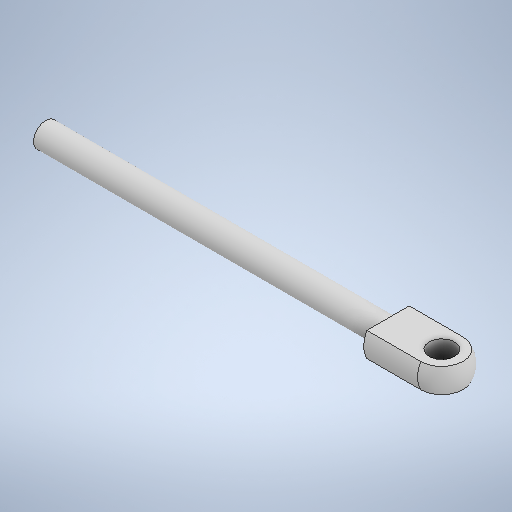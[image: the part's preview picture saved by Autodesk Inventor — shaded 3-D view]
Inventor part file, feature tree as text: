
AUTODESK INVENTOR PART (.ipt)
format: ipt  version: 2025.1 (Build 291241000, 241)  size: 287,744 bytes
history: native  units: mm
features: sketch x3, revolve x1, plane x1, extrude x1, hole x1
ambient origin geometry x8: Origin, YZ Plane, XZ Plane, XY Plane, X Axis, Y Axis, Z Axis, Center Point
bodies: Solid1 (feature_tree)
feature tree (7):
  revolve  "Revolution1"  [1 undecoded]
  plane  "Work Plane1"
  extrude  "Extrusion2"  Depth=40.5mm
  hole  "Hole1"  [1 undecoded]
  sketch  "Sketch1"  dims[d0=2.5mm d1=5.5mm]
  sketch  "Sketch2"  dims[d2=2.5mm d3=40.5mm]
  sketch  "Sketch3"  dims[d4=90.0deg d5=5.0mm d6=2.5mm d9=2.5mm d10=1.25mm d11=10.0mm d12=0.0mm d13=2.6mm d14=6.0mm d15=4.0mm d16=2.0mm d17=90.0deg d18=8.0mm d19=0.0mm]
note: 2 required parameter values undecoded (feature->parameter linkage not recoverable at this tier; creation-order binding heuristic only, values carry confidence <= 0.55)